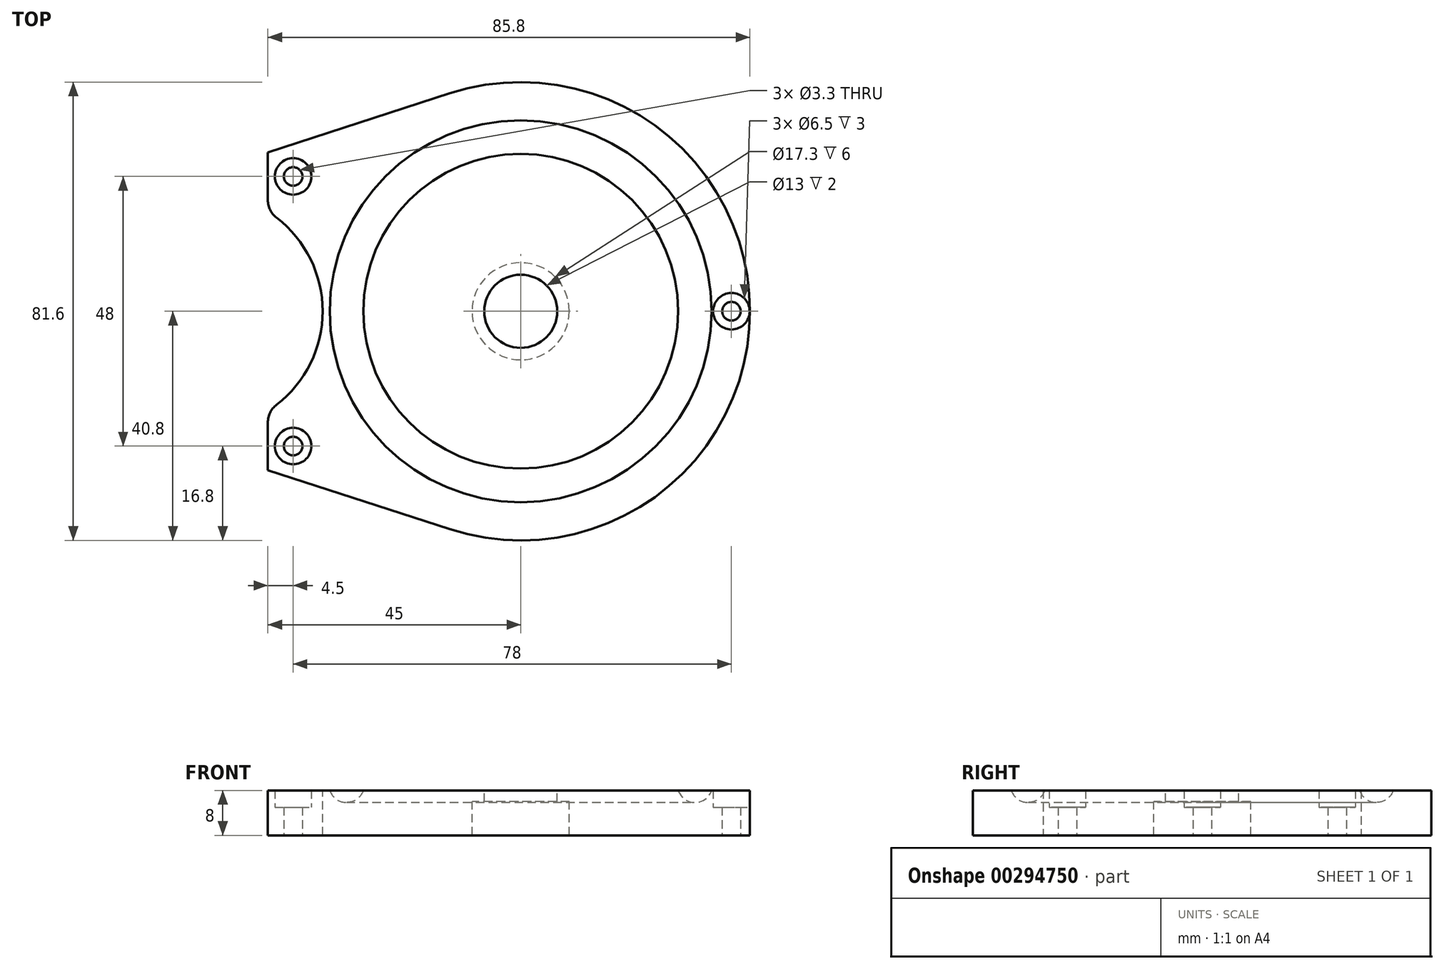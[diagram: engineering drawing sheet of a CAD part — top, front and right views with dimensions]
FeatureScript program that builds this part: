
annotation { "Feature Type Name" : "Feature", "Feature Type Description" : "" }
export const myFeature = defineFeature(function(context is Context, id is Id, definition is map)
    precondition{}
    {
        {
            var Q0;
            Q0=qCreatedBy(makeId("Top.planeOp"),FACE);
            var sketch = newSketch(context, id + "F0", { "sketchPlane" : qUnion([Q0])});
            skCircle(sketch, "E0", {"center": v(0, 0) * mm, "radius": 40.8 * mm});
            skSolve(sketch);
        }
        {
            var Q0;
            Q0 = qSketchRegion(id + "F0", true);
            extrude(context, id + "F1", {"entities" : qUnion([Q0]), "depth" : 8 * mm});
        }
        {
            var Q0;
            Q0=qCreatedBy(makeId("Right.planeOp"),FACE);
            var sketch = newSketch(context, id + "F2", { "sketchPlane" : qUnion([Q0])});
            skLineSegment(sketch, "E1", {"start": v(0, 0) * mm, "end": v(0, 8) * mm});
            skLineSegment(sketch, "E2", {"start": v(0, 8) * mm, "end": v(6.5, 8) * mm});
            skLineSegment(sketch, "E3", {"start": v(6.5, 8) * mm, "end": v(6.5, 6) * mm});
            skLineSegment(sketch, "E4", {"start": v(6.5, 6) * mm, "end": v(8.65, 6) * mm});
            skLineSegment(sketch, "E5", {"start": v(8.65, 6) * mm, "end": v(8.65, 0) * mm});
            skLineSegment(sketch, "E6", {"start": v(8.65, 0) * mm, "end": v(0, 0) * mm});
            skLineSegment(sketch, "E7", {"start": v(0, 8) * mm, "end": v(0, 13.47) * mm, "construction": true});
            skSolve(sketch);
        }
        {
            var Q0;
            Q0 = qSketchRegion(id + "F2", true);
            var Q1;
            Q1=sQuery(id+"F2.wireOp",EDGE,"E7");
            revolve(context, id + "F3", {"operationType" : NewBodyOperationType.REMOVE, "entities" : qUnion([Q0]), "axis" : qUnion([Q1]), "revolveType" : RevolveType.FULL, "oppositeDirection" : true});
        }
        {
            var Q0;
            Q0=qCreatedBy(makeId("Right.planeOp"),FACE);
            var sketch = newSketch(context, id + "F4", { "sketchPlane" : qUnion([Q0])});
            skCircle(sketch, "E8", {"center": v(31, 9) * mm, "radius": 3.15 * mm});
            skLineSegment(sketch, "E9", {"start": v(0, -0.8) * mm, "end": v(0, 13.57) * mm, "construction": true});
            skSolve(sketch);
        }
        {
            var Q0;
            Q0 = qSketchRegion(id + "F4", true);
            var Q1;
            Q1=sQuery(id+"F4.wireOp",EDGE,"E9");
            revolve(context, id + "F5", {"operationType" : NewBodyOperationType.REMOVE, "entities" : qUnion([Q0]), "axis" : qUnion([Q1]), "revolveType" : RevolveType.FULL, "oppositeDirection" : true});
        }
        {
            var Q0;
            Q0=qCreatedBy(makeId("Top.planeOp"),FACE);
            var sketch = newSketch(context, id + "F6", { "sketchPlane" : qUnion([Q0])});
            skLineSegment(sketch, "E10.bottom", {"start": v(-36, 19.2) * mm, "end": v(-40.8, 19.2) * mm});
            skLineSegment(sketch, "E10.top", {"start": v(-36, -19.2) * mm, "end": v(-40.8, -19.2) * mm});
            skLineSegment(sketch, "E10.left", {"start": v(-36, 19.2) * mm, "end": v(-36, -19.2) * mm});
            skLineSegment(sketch, "E10.right", {"start": v(-40.8, 19.2) * mm, "end": v(-40.8, -19.2) * mm});
            skSolve(sketch);
        }
        {
            var Q0;
            Q0 = qSketchRegion(id + "F6", true);
            extrude(context, id + "F7", {"entities" : qUnion([Q0]), "operationType" : NewBodyOperationType.REMOVE, "endBound" : BoundingType.THROUGH_ALL, "depth" : 25 * mm});
        }
        {
            var Q0;
            Q0=qCreatedBy(makeId("Top.planeOp"),FACE);
            var sketch = newSketch(context, id + "F8", { "sketchPlane" : qUnion([Q0])});
            skLineSegment(sketch, "E11", {"start": v(-45, -28.28) * mm, "end": v(-45, 28.28) * mm});
            skLineSegment(sketch, "E12", {"start": v(-45, 28.28) * mm, "end": v(-12.6, 38.8) * mm});
            skLineSegment(sketch, "E13", {"start": v(0, 0) * mm, "end": v(-51.86, 0) * mm, "construction": true});
            skArc(sketch, "E14.0", {"start": v(-12.6, 38.8) * mm, "mid": v(-26.2, 31.27) * mm, "end": v(-36, 19.2) * mm});
            skPoint(sketch, "E15.orphan", {"position": v(-36, -19.2) * mm});
            skLineSegment(sketch, "E16.MirrorCS", {"start": v(-45, -28.28) * mm, "end": v(-12.6, -38.8) * mm});
            skArc(sketch, "E17.MirrorCS", {"start": v(-12.6, -38.8) * mm, "mid": v(-26.2, -31.27) * mm, "end": v(-36, -19.2) * mm});
            skLineSegment(sketch, "E18", {"start": v(-36, 19.2) * mm, "end": v(-36, -19.2) * mm});
            skSolve(sketch);
        }
        {
            var Q0;
            Q0 = qSketchRegion(id + "F8", true);
            var Q1;
            {var subQ0=sQuery(id+"F0.wireOp",EDGE,"E0");Q1=makeQuery(id+"F5.boolean.opBoolean","SPLIT",FACE,{"disambiguationData":[TD([makeQuery(id+"F1.opExtrude","SWEPT_FACE",FACE,{"disambiguationData":[OSD([subQ0])]})])],"derivedFrom":makeQuery(id+"F1.opExtrude","CAP_FACE",FACE,{"disambiguationData":[OSD([subQ0])],"isStart":false})});}
            extrude(context, id + "F9", {"entities" : qUnion([Q0]), "operationType" : NewBodyOperationType.ADD, "endBound" : BoundingType.UP_TO_SURFACE, "endBoundEntityFace" : qUnion([Q1]), "depth" : 25 * mm});
        }
        {
            var Q0;
            {var subQ0=sQuery(id+"F0.wireOp",EDGE,"E0");Q0=makeQuery(id+"F9.boolean.opBoolean","MERGE",FACE,{"derivedFrom":[makeQuery(id+"F5.boolean.opBoolean","SPLIT",FACE,{"disambiguationData":[TD([makeQuery(id+"F1.opExtrude","SWEPT_FACE",FACE,{"disambiguationData":[OSD([subQ0])]})])],"derivedFrom":makeQuery(id+"F1.opExtrude","CAP_FACE",FACE,{"disambiguationData":[OSD([subQ0])],"isStart":false})}),makeQuery(id+"F9.opExtrude","CAP_FACE",FACE,{"disambiguationData":[OSD([sQuery(id+"F8.wireOp",EDGE,"E11"),sQuery(id+"F8.wireOp",EDGE,"E12"),sQuery(id+"F8.wireOp",EDGE,"E14.0"),sQuery(id+"F8.wireOp",EDGE,"E16.MirrorCS"),sQuery(id+"F8.wireOp",EDGE,"E17.MirrorCS"),sQuery(id+"F8.wireOp",EDGE,"E18")])],"isStart":false})]});}
            var sketch = newSketch(context, id + "F10", { "sketchPlane" : qUnion([Q0])});
            skCircle(sketch, "E19", {"center": v(-56.25, 0) * mm, "radius": 21 * mm});
            skLineSegment(sketch, "E20", {"start": v(-56.25, 0) * mm, "end": v(0, 0) * mm, "construction": true});
            skSolve(sketch);
        }
        {
            var Q0;
            Q0 = qSketchRegion(id + "F10", true);
            extrude(context, id + "F11", {"entities" : qUnion([Q0]), "operationType" : NewBodyOperationType.REMOVE, "endBound" : BoundingType.THROUGH_ALL, "oppositeDirection" : true, "depth" : 25 * mm});
        }
        {
            var Q0;
            Q0=makeQuery(id+"F11.boolean.opBoolean","INTERSECT",EDGE,{"disambiguationData":[OD(1.0)],"derivedFrom":[makeQuery(id+"F9.opExtrude","SWEPT_FACE",FACE,{"disambiguationData":[OSD([sQuery(id+"F8.wireOp",EDGE,"E11")])]}),makeQuery(id+"F11.opExtrude","SWEPT_FACE",FACE,{"disambiguationData":[OSD([sQuery(id+"F10.wireOp",EDGE,"E19")])]})]});
            var Q1;
            Q1=makeQuery(id+"F11.boolean.opBoolean","INTERSECT",EDGE,{"disambiguationData":[OD(0.0)],"derivedFrom":[makeQuery(id+"F9.opExtrude","SWEPT_FACE",FACE,{"disambiguationData":[OSD([sQuery(id+"F8.wireOp",EDGE,"E11")])]}),makeQuery(id+"F11.opExtrude","SWEPT_FACE",FACE,{"disambiguationData":[OSD([sQuery(id+"F10.wireOp",EDGE,"E19")])]})]});
            fillet(context, id + "F12", {"entities" : qUnion([Q0, Q1]), "radius" : 4 * mm, "tangentPropagation" : true, "allowEdgeOverflow" : false});
        }
        {
            var Q0;
            {var subQ0=sQuery(id+"F0.wireOp",EDGE,"E0");Q0=makeQuery(id+"F9.boolean.opBoolean","MERGE",FACE,{"derivedFrom":[makeQuery(id+"F5.boolean.opBoolean","SPLIT",FACE,{"disambiguationData":[TD([makeQuery(id+"F1.opExtrude","SWEPT_FACE",FACE,{"disambiguationData":[OSD([subQ0])]})])],"derivedFrom":makeQuery(id+"F1.opExtrude","CAP_FACE",FACE,{"disambiguationData":[OSD([subQ0])],"isStart":false})}),makeQuery(id+"F9.opExtrude","CAP_FACE",FACE,{"disambiguationData":[OSD([sQuery(id+"F8.wireOp",EDGE,"E11"),sQuery(id+"F8.wireOp",EDGE,"E12"),sQuery(id+"F8.wireOp",EDGE,"E14.0"),sQuery(id+"F8.wireOp",EDGE,"E16.MirrorCS"),sQuery(id+"F8.wireOp",EDGE,"E17.MirrorCS"),sQuery(id+"F8.wireOp",EDGE,"E18")])],"isStart":false})]});}
            var sketch = newSketch(context, id + "F13", { "sketchPlane" : qUnion([Q0])});
            skPoint(sketch, "E21", {"position": v(-40.5, 24) * mm});
            skPoint(sketch, "E22", {"position": v(37.5, 0) * mm});
            skLineSegment(sketch, "E23", {"start": v(0, 0) * mm, "end": v(47.97, 0) * mm, "construction": true});
            skPoint(sketch, "E24.MirrorP", {"position": v(-40.5, -24) * mm});
            skSolve(sketch);
        }
        {
            var Q0;
            Q0=sQuery(id+"F13.wireOp",VERTEX,"E21");
            var Q1;
            Q1=sQuery(id+"F13.wireOp",VERTEX,"E24.MirrorP");
            var Q2;
            Q2=sQuery(id+"F13.wireOp",VERTEX,"E22");
            var Q3;
            Q3=makeQuery(id+"F1.opExtrude","SWEPT_BODY",BODY,{"disambiguationData":[OSD([sQuery(id+"F0.wireOp",EDGE,"E0")])]});
            hole(context, id + "F14", {"style" : HoleStyle.C_BORE, "endStyle" : HoleEndStyle.THROUGH, "standardTappedOrClearance" : lookupTablePath({ "standard" : "ISO", "fit" : "Normal", "size" : "M3", "type" : "Clearance" }), "standardBlindInLast" : lookupTablePath({ "fit" : "Standard", "standard" : "ISO", "size" : "M3", "type" : "Clearance" }), "holeDiameter" : 3.3 * mm, "cBoreDiameter" : 6.5 * mm, "cBoreDepth" : 3 * mm, "tappedDepth" : 12 * mm, "tapClearance" : 3, "locations" : qUnion([Q0, Q1, Q2]), "scope" : qUnion([Q3])});
        }
    });
